# Revit family: ВКП_1000х500_Eng
name_source: partatom
category: Mechanical Equipment
units: mm (PartAtom-declared; Revit-internal decimal feet)

## family parameters
Always vertical = Yes
Classification = None
Cut with Voids When Loaded = No
Part Type = Normal
Room Calculation Point = No
Round Connector Dimension = Use Diameter
Shared = No
Work Plane-Based = No

## types (2) — shared parameters
00_20_Manufacturer = Vents
00_20_Name = Inline centrifugal fan
B = 1000 mm  [stored 3.28084 ft]
B1 = 1020 mm  [stored 3.34646 ft]
B2 = 1040 mm  [stored 3.41207 ft]
Casing Material = Steel, galvanized
Description = For rectangular ducts
H = 500 mm  [stored 1.64042 ft]
H1 = 520 mm  [stored 1.70604 ft]
H2 = 540 mm  [stored 1.77165 ft]
Height = 730 mm
L = 1150 mm  [stored 3.77297 ft]
Length = 1150 mm  [stored 3.77297 ft]
Load Classification = HVAC
Maintenance zone material = <By Category>
Manufacturer = Vents
Number of Fase = 3
URL = https://ventilation-system.com
Voltage = 400 V
Width = 1040 mm  [stored 3.41207 ft]
h1 = 250 mm  [stored 0.82021 ft]
zero-valued in all types: Default Elevation

## per-type parameters (varying)
| type | Amperage | Maximum Air Flow | Power | Weight |
| VKP 4D 1000x500 | 7 A | 4170.0 L/s | 4300 W | 126 kg |
| VKP 6D 1000x500 | 3 A | 2900.0 L/s | 1198 W | 120 kg |

note: column(s) folded — value = type name in every type: 00_20_Type

note: [stored X ft] marks values corroborated as IEEE doubles in the binary element streams (Revit-internal decimal feet)
